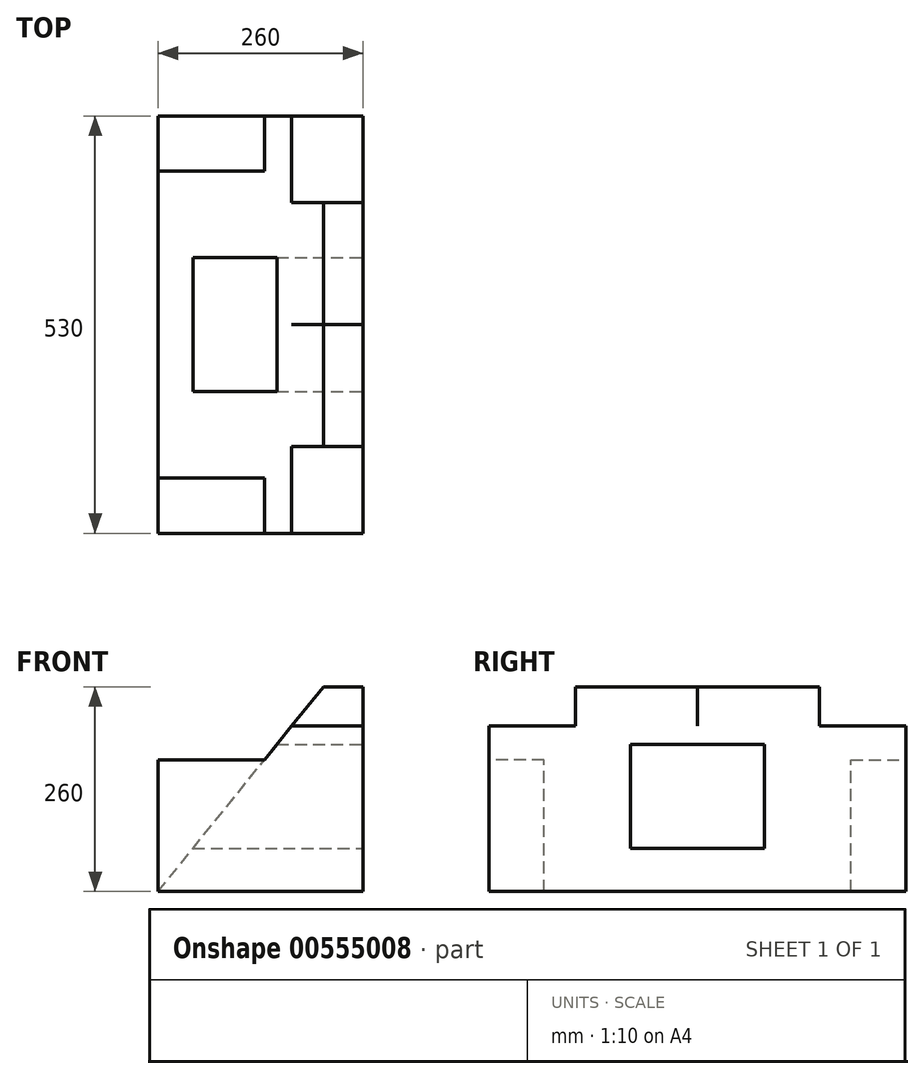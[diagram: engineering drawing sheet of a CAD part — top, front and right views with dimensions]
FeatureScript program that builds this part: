
annotation { "Feature Type Name" : "Feature", "Feature Type Description" : "" }
export const myFeature = defineFeature(function(context is Context, id is Id, definition is map)
    precondition{}
    {
        {
            var Q0;
            Q0=qCreatedBy(makeId("Front.planeOp"),FACE);
            var sketch = newSketch(context, id + "F0", { "sketchPlane" : qUnion([Q0])});
            skLineSegment(sketch, "E0", {"start": v(0, 0) * mm, "end": v(210, 260) * mm});
            skLineSegment(sketch, "E1", {"start": v(210, 260) * mm, "end": v(260, 260) * mm});
            skLineSegment(sketch, "E2", {"start": v(0, 0) * mm, "end": v(260, 0) * mm});
            skLineSegment(sketch, "E3", {"start": v(260, 210) * mm, "end": v(169.62, 210) * mm});
            skLineSegment(sketch, "E4", {"start": v(260, 260) * mm, "end": v(260, 210) * mm});
            skLineSegment(sketch, "E5", {"start": v(260, 0) * mm, "end": v(260, 210) * mm});
            skLineSegment(sketch, "E6", {"start": v(0, 0) * mm, "end": v(0, 167) * mm});
            skLineSegment(sketch, "E7", {"start": v(0, 167) * mm, "end": v(134.88, 167) * mm});
            skSolve(sketch);
        }
        {
            var Q0;
            {var subQ0=sQuery(id+"F0.wireOp",EDGE,"E2");Q0=makeQuery(id+"F0.imprint","IMPRINT",FACE,{"disambiguationData":[TD([[makeQuery(id+"F0.imprint","IMPRINT",EDGE,{"derivedFrom":subQ0}),1.0]])]});}
            extrude(context, id + "F1", {"entities" : qUnion([Q0]), "depth" : 265 * mm});
        }
        {
            var Q0;
            {var subQ0=sQuery(id+"F0.wireOp",EDGE,"E6");Q0=makeQuery(id+"F0.imprint","IMPRINT",FACE,{"disambiguationData":[TD([[makeQuery(id+"F0.imprint","IMPRINT",EDGE,{"derivedFrom":subQ0}),-1.0]])]});}
            extrude(context, id + "F2", {"entities" : qUnion([Q0]), "operationType" : NewBodyOperationType.ADD, "depth" : 70 * mm});
        }
        {
            var Q0;
            {var subQ0=sQuery(id+"F0.wireOp",EDGE,"E1");Q0=makeQuery(id+"F0.imprint","IMPRINT",FACE,{"disambiguationData":[TD([[makeQuery(id+"F0.imprint","IMPRINT",EDGE,{"derivedFrom":subQ0}),-1.0]])]});}
            extrude(context, id + "F3", {"entities" : qUnion([Q0]), "depth" : 264.92 * mm});
        }
        {
            var Q0;
            Q0=makeQuery(id+"F3.opExtrude","CAP_FACE",FACE,{"disambiguationData":[OSD([sQuery(id+"F0.wireOp",EDGE,"E0"),sQuery(id+"F0.wireOp",EDGE,"E1"),sQuery(id+"F0.wireOp",EDGE,"E3"),sQuery(id+"F0.wireOp",EDGE,"E4")])],"isStart":true});
            extrude(context, id + "F4", {"entities" : qUnion([Q0]), "operationType" : NewBodyOperationType.REMOVE, "oppositeDirection" : true, "depth" : 110 * mm});
        }
        {
            var Q0;
            Q0=makeQuery(id+"F1.opExtrude","CAP_FACE",FACE,{"disambiguationData":[OSD([sQuery(id+"F0.wireOp",EDGE,"E0"),sQuery(id+"F0.wireOp",EDGE,"E2"),sQuery(id+"F0.wireOp",EDGE,"E3"),sQuery(id+"F0.wireOp",EDGE,"E5")])],"isStart":false});
            var sketch = newSketch(context, id + "F5", { "sketchPlane" : qUnion([Q0])});
            skLineSegment(sketch, "E8", {"start": v(150.8, 186.7) * mm, "end": v(260, 186.7) * mm});
            skLineSegment(sketch, "E9", {"start": v(43.98, 54.46) * mm, "end": v(260, 54.46) * mm});
            skLineSegment(sketch, "E10", {"start": v(43.98, 54.46) * mm, "end": v(150.8, 186.7) * mm});
            skLineSegment(sketch, "E11", {"start": v(43.98, 54.46) * mm, "end": v(0, 0) * mm});
            skSolve(sketch);
        }
        {
            var Q0;
            {var subQ0=sQuery(id+"F5.wireOp",EDGE,"E8");Q0=makeQuery(id+"F5.imprint","IMPRINT",FACE,{"disambiguationData":[TD([[makeQuery(id+"F5.imprint","IMPRINT",EDGE,{"derivedFrom":subQ0}),-1.0]])]});}
            extrude(context, id + "F6", {"entities" : qUnion([Q0]), "operationType" : NewBodyOperationType.REMOVE, "oppositeDirection" : true, "depth" : 85 * mm, "offsetDistance" : 25.4 * mm});
        }
        {
            var Q0;
            Q0=makeQuery(id+"F1.opExtrude","SWEPT_BODY",BODY,{"disambiguationData":[OSD([sQuery(id+"F0.wireOp",EDGE,"E0"),sQuery(id+"F0.wireOp",EDGE,"E2"),sQuery(id+"F0.wireOp",EDGE,"E3"),sQuery(id+"F0.wireOp",EDGE,"E5")])]});
            var Q1;
            Q1=makeQuery(id+"F3.opExtrude","SWEPT_BODY",BODY,{"disambiguationData":[OSD([sQuery(id+"F0.wireOp",EDGE,"E0"),sQuery(id+"F0.wireOp",EDGE,"E1"),sQuery(id+"F0.wireOp",EDGE,"E3"),sQuery(id+"F0.wireOp",EDGE,"E4")])]});
            var Q2;
            {var subQ0=sQuery(id+"F0.wireOp",EDGE,"E0");var subQ1=sQuery(id+"F0.wireOp",EDGE,"E5");var subQ2=sQuery(id+"F0.wireOp",EDGE,"E2");Q2=makeQuery(id+"F6.boolean.opBoolean","SPLIT",FACE,{"disambiguationData":[TD([makeQuery(id+"F1.opExtrude","SWEPT_FACE",FACE,{"disambiguationData":[OSD([subQ2])]})])],"derivedFrom":makeQuery(id+"F1.opExtrude","CAP_FACE",FACE,{"disambiguationData":[OSD([subQ0,subQ2,sQuery(id+"F0.wireOp",EDGE,"E3"),subQ1])],"isStart":false})});}
            mirror(context, id + "F7", {"operationType" : NewBodyOperationType.ADD, "entities" : qUnion([Q0, Q1]), "mirrorPlane" : qUnion([Q2])});
        }
    });
